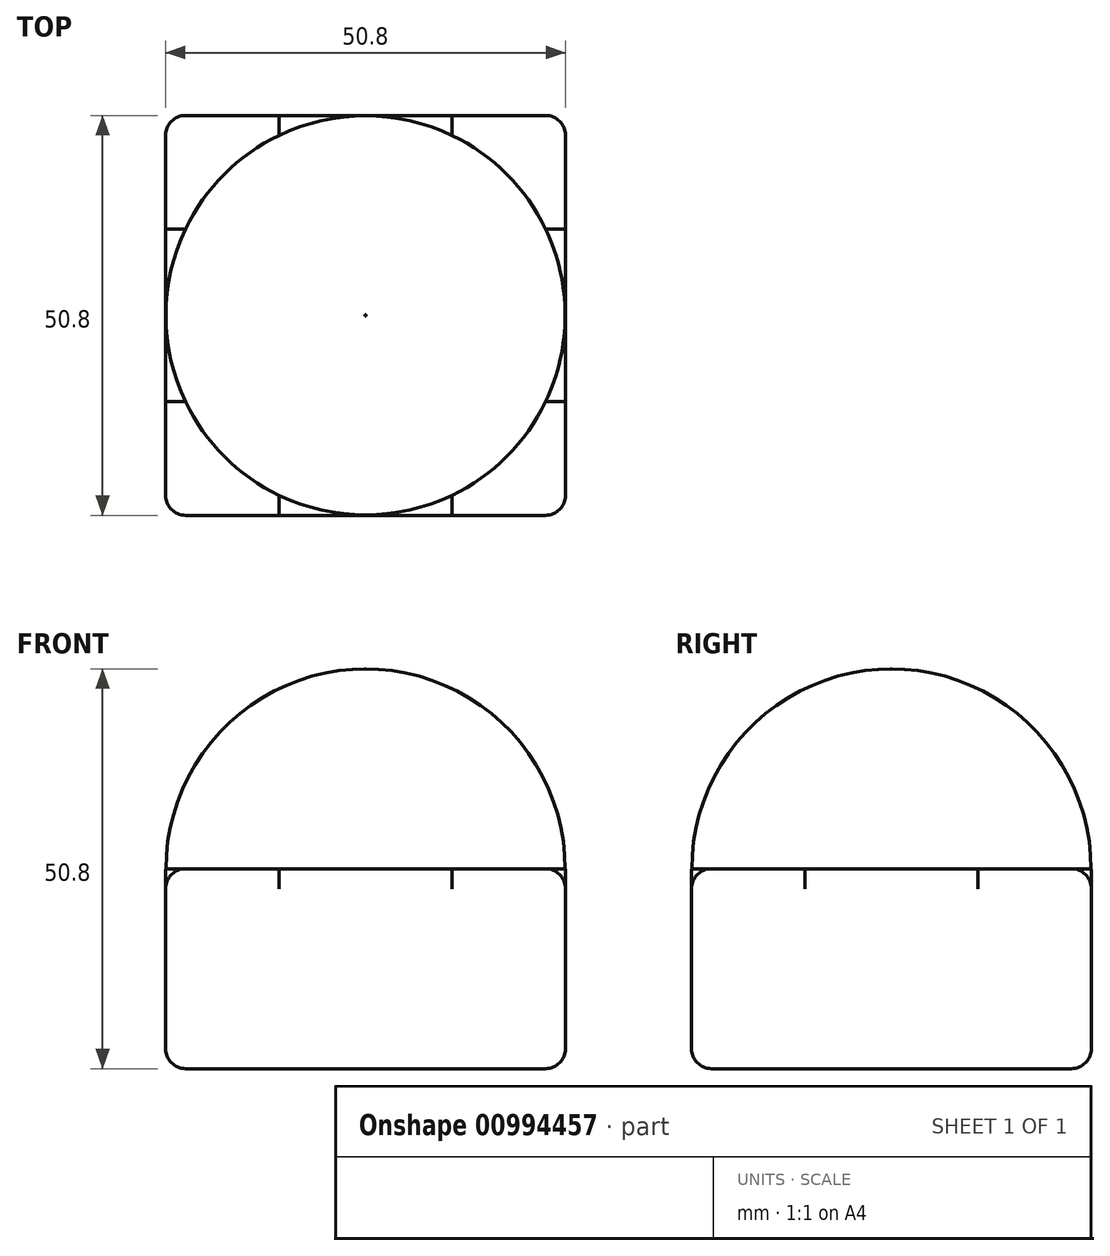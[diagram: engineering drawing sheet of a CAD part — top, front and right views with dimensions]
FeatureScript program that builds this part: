
annotation { "Feature Type Name" : "Feature", "Feature Type Description" : "" }
export const myFeature = defineFeature(function(context is Context, id is Id, definition is map)
    precondition{}
    {
        {
            var Q0;
            Q0=qCreatedBy(makeId("Front.planeOp"),FACE);
            var sketch = newSketch(context, id + "F0", { "sketchPlane" : qUnion([Q0])});
            skLineSegment(sketch, "E0", {"start": v(0, 25.4) * mm, "end": v(0, -25.4) * mm});
            skArc(sketch, "E1", {"start": v(0, -25.4) * mm, "mid": v(25.36, 0) * mm, "end": v(0, 25.4) * mm});
            skSolve(sketch);
        }
        {
            var Q0;
            Q0=makeQuery(id+"F0.imprint","IMPRINT",FACE,{"disambiguationData":[TD([[makeQuery(id+"F0.imprint","IMPRINT",EDGE,{"derivedFrom":sQuery(id+"F0.wireOp",EDGE,"E0")}),1.0]])]});
            var Q1;
            Q1=sQuery(id+"F0.wireOp",EDGE,"E0");
            revolve(context, id + "F1", {"surfaceOperationType" : NewSurfaceOperationType.NEW, "entities" : qUnion([Q0]), "axis" : qUnion([Q1]), "revolveType" : RevolveType.SYMMETRIC, "oppositeDirection" : true, "angle" : 360 * degree});
        }
        {
            var Q0;
            Q0=qCreatedBy(makeId("Front.planeOp"),FACE);
            var sketch = newSketch(context, id + "F2", { "sketchPlane" : qUnion([Q0])});
            skLineSegment(sketch, "E2.bottom", {"start": v(-25.4, 0) * mm, "end": v(25.4, 0) * mm});
            skLineSegment(sketch, "E2.top", {"start": v(-25.4, -25.4) * mm, "end": v(25.4, -25.4) * mm});
            skLineSegment(sketch, "E2.left", {"start": v(-25.4, 0) * mm, "end": v(-25.4, -25.4) * mm});
            skLineSegment(sketch, "E2.right", {"start": v(25.4, 0) * mm, "end": v(25.4, -25.4) * mm});
            skSolve(sketch);
        }
        {
            var Q0;
            Q0=makeQuery(id+"F2.imprint","IMPRINT",FACE,{"disambiguationData":[TD([[makeQuery(id+"F2.imprint","IMPRINT",EDGE,{"derivedFrom":sQuery(id+"F2.wireOp",EDGE,"E2.bottom")}),-1.0]])]});
            extrude(context, id + "F3", {"entities" : qUnion([Q0]), "operationType" : NewBodyOperationType.ADD, "endBound" : BoundingType.SYMMETRIC, "depth" : 50.8 * mm, "offsetDistance" : 25.4 * mm});
        }
        {
            var Q0;
            Q0=makeQuery(id+"F3.opExtrude","CAP_EDGE",EDGE,{"disambiguationData":[OSD([sQuery(id+"F2.wireOp",EDGE,"E2.left")])],"isStart":false});
            var Q1;
            Q1=makeQuery(id+"F3.opExtrude","SWEPT_EDGE",EDGE,{"disambiguationData":[OSD([sQuery(id+"F2.wireOp",EDGE,"E2.bottom"),sQuery(id+"F2.wireOp",EDGE,"E2.left")])]});
            var Q2;
            Q2=makeQuery(id+"F3.opExtrude","CAP_EDGE",EDGE,{"disambiguationData":[OSD([sQuery(id+"F2.wireOp",EDGE,"E2.bottom")])],"isStart":false});
            var Q3;
            Q3=makeQuery(id+"F3.opExtrude","CAP_EDGE",EDGE,{"disambiguationData":[OSD([sQuery(id+"F2.wireOp",EDGE,"E2.top")])],"isStart":false});
            var Q4;
            Q4=makeQuery(id+"F3.opExtrude","SWEPT_EDGE",EDGE,{"disambiguationData":[OSD([sQuery(id+"F2.wireOp",EDGE,"E2.top"),sQuery(id+"F2.wireOp",EDGE,"E2.left")])]});
            var Q5;
            Q5=makeQuery(id+"F3.opExtrude","CAP_EDGE",EDGE,{"disambiguationData":[OSD([sQuery(id+"F2.wireOp",EDGE,"E2.left")])],"isStart":true});
            var Q6;
            Q6=makeQuery(id+"F3.opExtrude","CAP_EDGE",EDGE,{"disambiguationData":[OSD([sQuery(id+"F2.wireOp",EDGE,"E2.bottom")])],"isStart":true});
            var Q7;
            Q7=makeQuery(id+"F3.opExtrude","CAP_EDGE",EDGE,{"disambiguationData":[OSD([sQuery(id+"F2.wireOp",EDGE,"E2.top")])],"isStart":true});
            var Q8;
            Q8=makeQuery(id+"F3.opExtrude","CAP_EDGE",EDGE,{"disambiguationData":[OSD([sQuery(id+"F2.wireOp",EDGE,"E2.right")])],"isStart":true});
            var Q9;
            Q9=makeQuery(id+"F3.opExtrude","SWEPT_EDGE",EDGE,{"disambiguationData":[OSD([sQuery(id+"F2.wireOp",EDGE,"E2.bottom"),sQuery(id+"F2.wireOp",EDGE,"E2.right")])]});
            var Q10;
            Q10=makeQuery(id+"F3.opExtrude","SWEPT_EDGE",EDGE,{"disambiguationData":[OSD([sQuery(id+"F2.wireOp",EDGE,"E2.top"),sQuery(id+"F2.wireOp",EDGE,"E2.right")])]});
            var Q11;
            Q11=makeQuery(id+"F3.opExtrude","CAP_EDGE",EDGE,{"disambiguationData":[OSD([sQuery(id+"F2.wireOp",EDGE,"E2.right")])],"isStart":false});
            fillet(context, id + "F4", {"entities" : qUnion([Q0, Q1, Q2, Q3, Q4, Q5, Q6, Q7, Q8, Q9, Q10, Q11]), "radius" : 2.54 * mm, "tangentPropagation" : true, "allowEdgeOverflow" : false});
        }
    });
